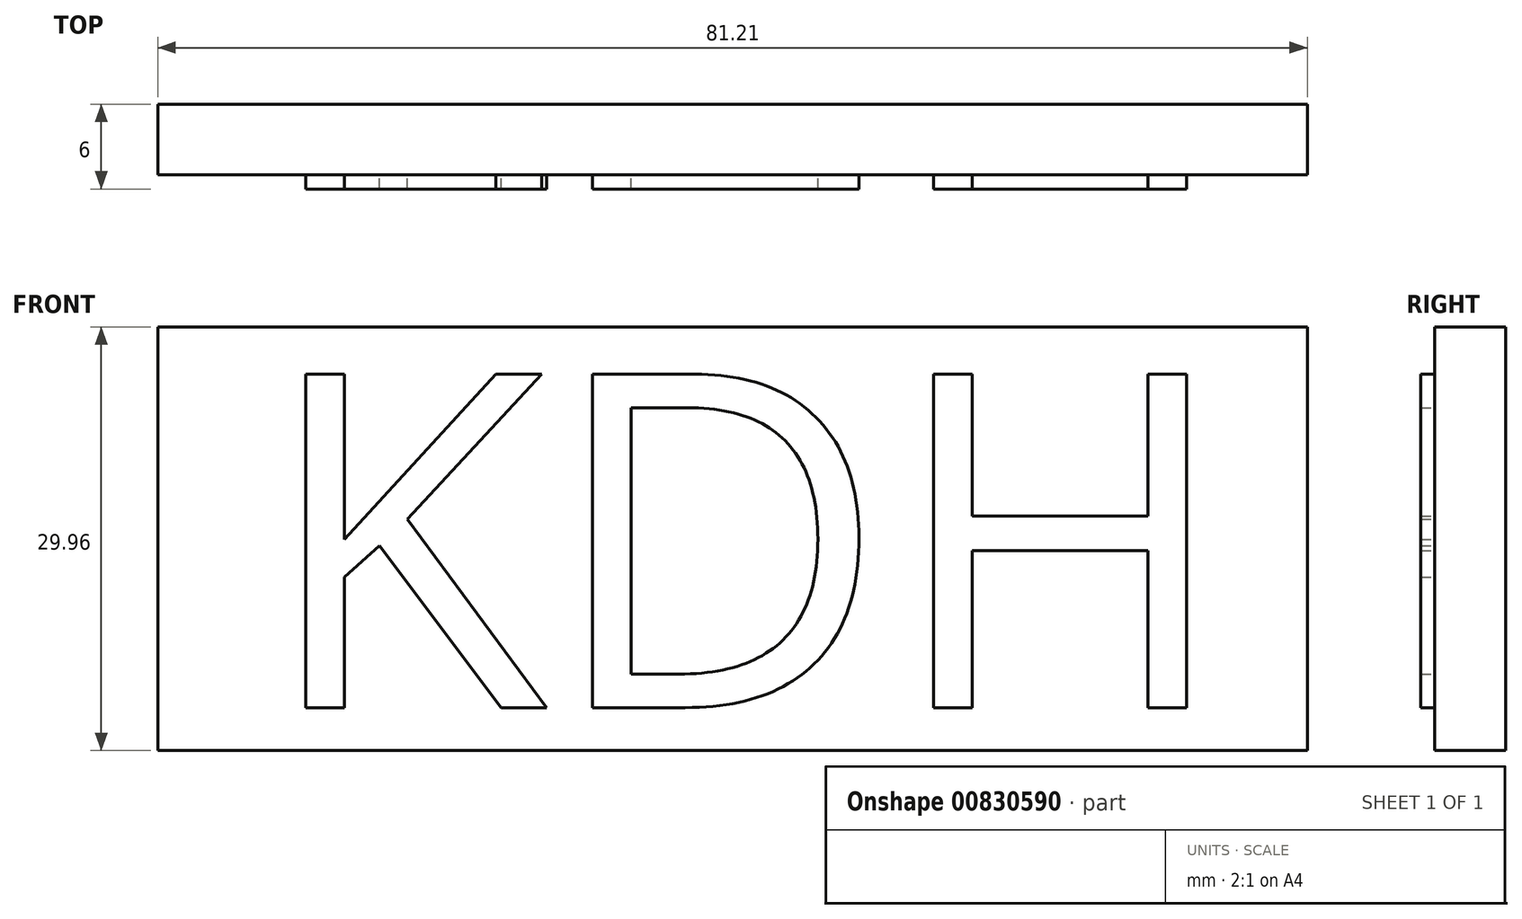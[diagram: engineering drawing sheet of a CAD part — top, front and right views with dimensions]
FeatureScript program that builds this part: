
annotation { "Feature Type Name" : "Feature", "Feature Type Description" : "" }
export const myFeature = defineFeature(function(context is Context, id is Id, definition is map)
    precondition{}
    {
        {
            var Q0;
            Q0=qCreatedBy(makeId("Front.planeOp"),FACE);
            var sketch = newSketch(context, id + "F0", { "sketchPlane" : qUnion([Q0])});
            skLineSegment(sketch, "E0.bottom", {"start": v(0, 0) * mm, "end": v(81.2, 0) * mm});
            skLineSegment(sketch, "E0.top", {"start": v(0, 29.96) * mm, "end": v(81.2, 29.96) * mm});
            skLineSegment(sketch, "E0.left", {"start": v(0, 0) * mm, "end": v(0, 29.96) * mm});
            skLineSegment(sketch, "E0.right", {"start": v(81.2, 0) * mm, "end": v(81.2, 29.96) * mm});
            skSolve(sketch);
        }
        {
            var Q0;
            Q0=makeQuery(id+"F0.imprint","IMPRINT",FACE,{"disambiguationData":[TD([[makeQuery(id+"F0.imprint","IMPRINT",EDGE,{"derivedFrom":sQuery(id+"F0.wireOp",EDGE,"E0.bottom")}),1.0]])]});
            extrude(context, id + "F1", {"entities" : qUnion([Q0]), "depth" : 5 * mm, "offsetDistance" : 25.4 * mm});
        }
        {
            var Q0;
            Q0=makeQuery(id+"F1.opExtrude","CAP_FACE",FACE,{"disambiguationData":[OSD([sQuery(id+"F0.wireOp",EDGE,"E0.bottom"),sQuery(id+"F0.wireOp",EDGE,"E0.top"),sQuery(id+"F0.wireOp",EDGE,"E0.left"),sQuery(id+"F0.wireOp",EDGE,"E0.right")])],"isStart":false});
            var sketch = newSketch(context, id + "F2", { "sketchPlane" : qUnion([Q0])});
            skText(sketch, "E1", { "text": "KDH", "fontName": "OpenSans-Regular.ttf"});
            const initialGuessF2  = {"E1": [0.0072, 0.00304, 1, 0, 0.02378]};
            skSetInitialGuess(sketch, initialGuessF2);
            skSolve(sketch);
        }
        {
            var Q0;
            Q0 = qSketchRegion(id + "F2", true);
            extrude(context, id + "F3", {"entities" : qUnion([Q0]), "operationType" : NewBodyOperationType.ADD, "depth" : 1 * mm, "offsetDistance" : 25.4 * mm});
        }
    });
